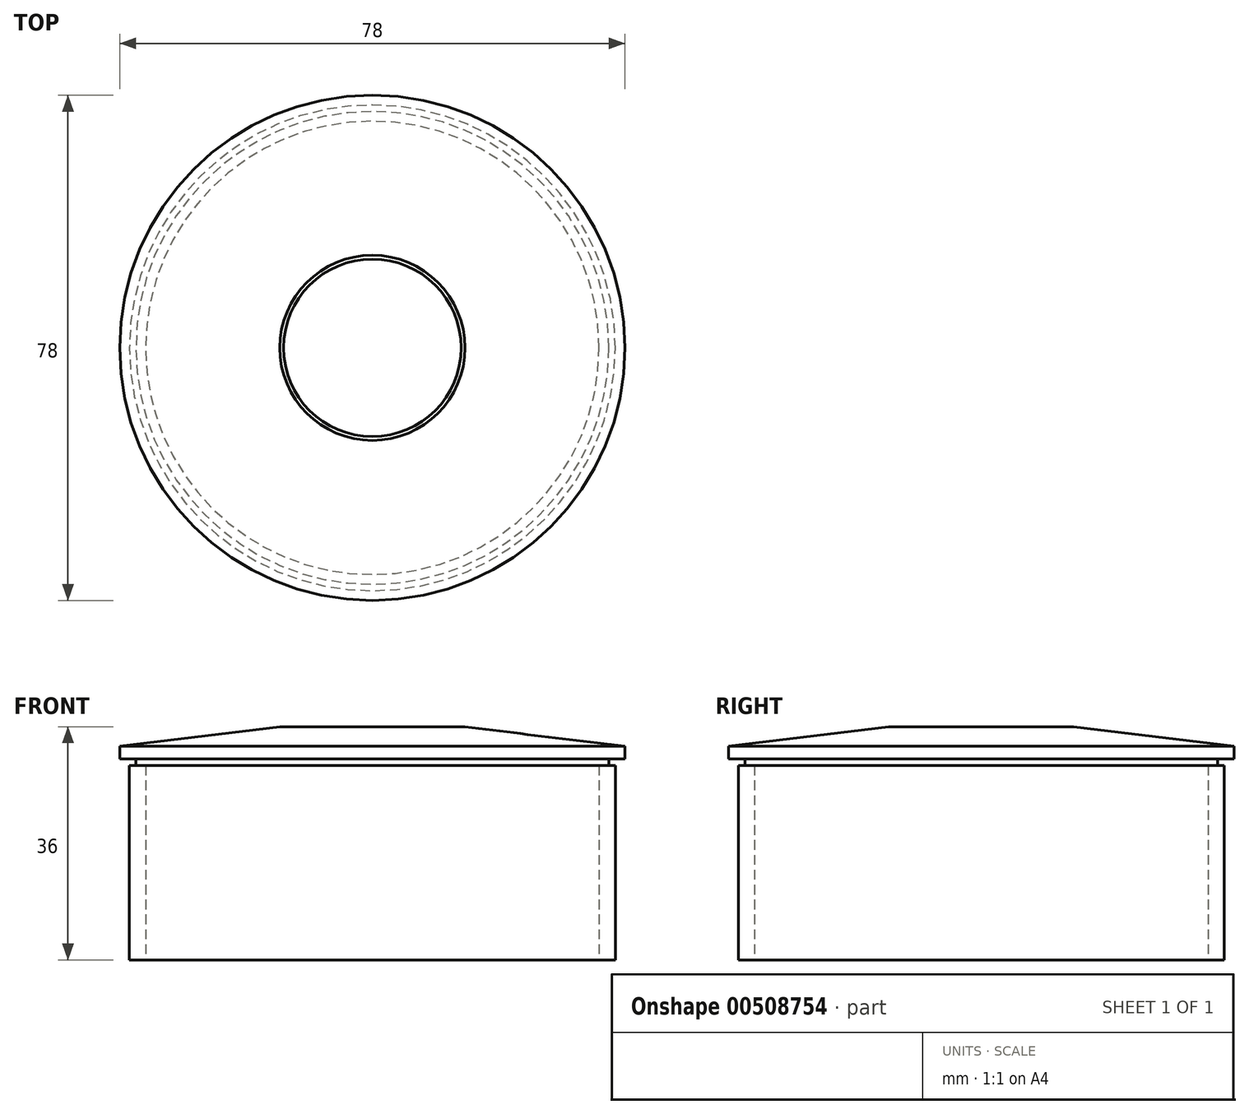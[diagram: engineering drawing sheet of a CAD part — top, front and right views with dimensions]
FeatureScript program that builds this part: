
annotation { "Feature Type Name" : "Feature", "Feature Type Description" : "" }
export const myFeature = defineFeature(function(context is Context, id is Id, definition is map)
    precondition{}
    {
        {
            var Q0;
            Q0=qCreatedBy(makeId("Top.planeOp"),FACE);
            var sketch = newSketch(context, id + "F0", { "sketchPlane" : qUnion([Q0])});
            skCircle(sketch, "E0", {"center": v(0, 0) * mm, "radius": 37.5 * mm});
            skCircle(sketch, "E1", {"center": v(0, 0) * mm, "radius": 35 * mm});
            skSolve(sketch);
        }
        {
            var Q0;
            Q0=makeQuery(id+"F0.imprint","IMPRINT",FACE,{"disambiguationData":[TD([[makeQuery(id+"F0.imprint","IMPRINT",EDGE,{"derivedFrom":sQuery(id+"F0.wireOp",EDGE,"E0")}),1.0]])]});
            extrude(context, id + "F1", {"entities" : qUnion([Q0]), "depth" : 30 * mm});
        }
        {
            var Q0;
            Q0=makeQuery(id+"F1.opExtrude","CAP_FACE",FACE,{"disambiguationData":[OSD([sQuery(id+"F0.wireOp",EDGE,"E0"),sQuery(id+"F0.wireOp",EDGE,"E1")])],"isStart":false});
            var sketch = newSketch(context, id + "F2", { "sketchPlane" : qUnion([Q0])});
            skCircle(sketch, "E2", {"center": v(0, 0) * mm, "radius": 36.5 * mm});
            skSolve(sketch);
        }
        {
            var Q0;
            Q0=makeQuery(id+"F2.imprint","IMPRINT",FACE,{"disambiguationData":[TD([[makeQuery(id+"F2.imprint","IMPRINT",EDGE,{"derivedFrom":sQuery(id+"F2.wireOp",EDGE,"E2")}),1.0]])]});
            var Q1;
            Q1=makeQuery(id+"F2.imprint","IMPRINT",FACE,{"disambiguationData":[TD([[makeQuery(id+"F2.imprint","IMPRINT",EDGE,{"derivedFrom":makeQuery(id+"F1.opExtrude","CAP_EDGE",EDGE,{"disambiguationData":[OSD([sQuery(id+"F0.wireOp",EDGE,"E1")])],"isStart":false})}),1.0]])]});
            extrude(context, id + "F3", {"entities" : qUnion([Q0, Q1]), "operationType" : NewBodyOperationType.ADD, "depth" : 1 * mm});
        }
        {
            var Q0;
            Q0=makeQuery(id+"F3.opExtrude","CAP_FACE",FACE,{"disambiguationData":[OSD([sQuery(id+"F2.wireOp",EDGE,"E2")])],"isStart":false});
            var sketch = newSketch(context, id + "F4", { "sketchPlane" : qUnion([Q0])});
            skCircle(sketch, "E3", {"center": v(0, 0) * mm, "radius": 39 * mm});
            skSolve(sketch);
        }
        {
            var Q0;
            Q0=makeQuery(id+"F4.imprint","IMPRINT",FACE,{"disambiguationData":[TD([[makeQuery(id+"F4.imprint","IMPRINT",EDGE,{"derivedFrom":makeQuery(id+"F3.opExtrude","CAP_EDGE",EDGE,{"disambiguationData":[OSD([sQuery(id+"F2.wireOp",EDGE,"E2")])],"isStart":false})}),1.0]])]});
            var Q1;
            Q1=makeQuery(id+"F4.imprint","IMPRINT",FACE,{"disambiguationData":[TD([[makeQuery(id+"F4.imprint","IMPRINT",EDGE,{"derivedFrom":sQuery(id+"F4.wireOp",EDGE,"E3")}),1.0]])]});
            extrude(context, id + "F5", {"entities" : qUnion([Q0, Q1]), "operationType" : NewBodyOperationType.ADD, "depth" : 5 * mm});
        }
        {
            var Q0;
            Q0=makeQuery(id+"F5.opExtrude","CAP_EDGE",EDGE,{"disambiguationData":[OSD([sQuery(id+"F4.wireOp",EDGE,"E3")])],"isStart":false});
            chamfer(context, id + "F6", {"entities" : qUnion([Q0]), "chamferType" : ChamferType.TWO_OFFSETS, "width1" : 25 * mm, "oppositeDirection" : false, "width2" : 3 * mm, "tangentPropagation" : true});
        }
        {
            var Q0;
            Q0=makeQuery(id+"F5.opExtrude","CAP_FACE",FACE,{"disambiguationData":[OSD([sQuery(id+"F4.wireOp",EDGE,"E3")])],"isStart":false});
            chamfer(context, id + "F7", {"entities" : qUnion([Q0]), "width" : 5 * mm, "tangentPropagation" : true});
        }
    });
